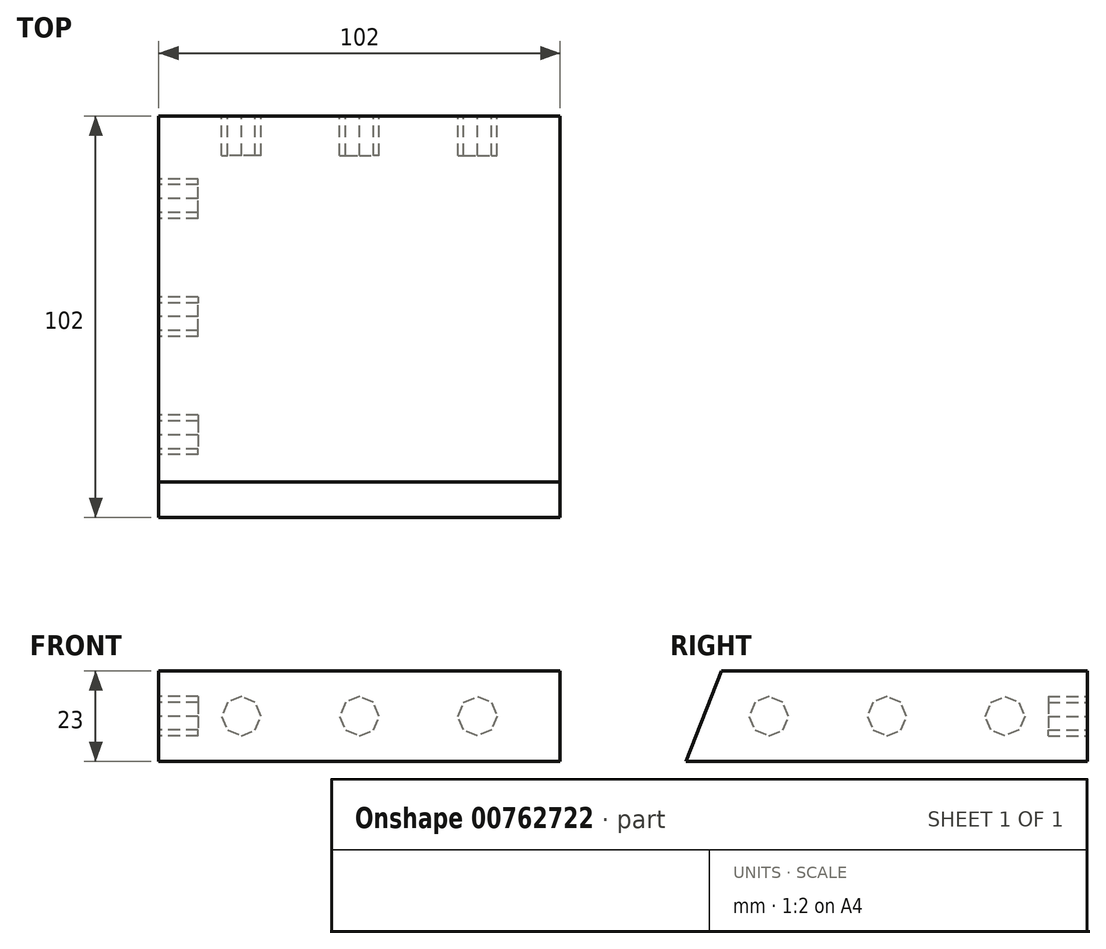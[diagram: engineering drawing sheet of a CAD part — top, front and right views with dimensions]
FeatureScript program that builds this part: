
annotation { "Feature Type Name" : "Feature", "Feature Type Description" : "" }
export const myFeature = defineFeature(function(context is Context, id is Id, definition is map)
    precondition{}
    {
        {
            var Q0;
            Q0=qCreatedBy(makeId("Right.planeOp"),FACE);
            var sketch = newSketch(context, id + "F0", { "sketchPlane" : qUnion([Q0])});
            skLineSegment(sketch, "E0.bottom", {"start": v(51, -11.5) * mm, "end": v(-51, -11.5) * mm});
            skLineSegment(sketch, "E0.top", {"start": v(51, 11.5) * mm, "end": v(-42, 11.5) * mm});
            skLineSegment(sketch, "E0.left", {"start": v(51, -11.5) * mm, "end": v(51, 11.5) * mm});
            skPoint(sketch, "E0.middle", {"position": v(0, 0) * mm});
            skLineSegment(sketch, "E1", {"start": v(-42, 11.5) * mm, "end": v(-51, -11.5) * mm});
            skPoint(sketch, "E0.right.end.orphan", {"position": v(-51, 11.5) * mm});
            skSolve(sketch);
        }
        {
            var Q0;
            Q0 = qSketchRegion(id + "F0", true);
            extrude(context, id + "F1", {"entities" : qUnion([Q0]), "endBound" : BoundingType.SYMMETRIC, "depth" : 102 * mm, "offsetDistance" : 25 * mm});
        }
        {
            var Q0;
            Q0=makeQuery(id+"F1.opExtrude","SWEPT_FACE",FACE,{"disambiguationData":[OSD([sQuery(id+"F0.wireOp",EDGE,"E0.left")])]});
            var sketch = newSketch(context, id + "F2", { "sketchPlane" : qUnion([Q0])});
            skCircle(sketch, "E2.cCircle", {"center": v(0, 0) * mm, "radius": 5 * mm, "construction": true});
            skLineSegment(sketch, "E2.0", {"start": v(0, -5) * mm, "end": v(-3.54, -3.54) * mm});
            skLineSegment(sketch, "E2.1", {"start": v(-3.54, -3.54) * mm, "end": v(-5, 0) * mm});
            skLineSegment(sketch, "E2.2", {"start": v(-5, 0) * mm, "end": v(-3.54, 3.54) * mm});
            skLineSegment(sketch, "E2.3", {"start": v(-3.54, 3.54) * mm, "end": v(0, 5) * mm});
            skLineSegment(sketch, "E2.4", {"start": v(0, 5) * mm, "end": v(3.54, 3.54) * mm});
            skLineSegment(sketch, "E2.5", {"start": v(3.54, 3.54) * mm, "end": v(5, 0) * mm});
            skLineSegment(sketch, "E2.6", {"start": v(5, 0) * mm, "end": v(3.54, -3.54) * mm});
            skLineSegment(sketch, "E2.7", {"start": v(3.54, -3.54) * mm, "end": v(0, -5) * mm});
            skLineSegment(sketch, "E3.1.0.0", {"start": v(30, 5) * mm, "end": v(33.54, 3.54) * mm});
            skLineSegment(sketch, "E3.1.0.1", {"start": v(33.54, 3.54) * mm, "end": v(35, 0) * mm});
            skLineSegment(sketch, "E3.1.0.2", {"start": v(35, 0) * mm, "end": v(33.54, -3.54) * mm});
            skLineSegment(sketch, "E3.1.0.3", {"start": v(33.54, -3.54) * mm, "end": v(30, -5) * mm});
            skLineSegment(sketch, "E3.1.0.4", {"start": v(30, -5) * mm, "end": v(26.46, -3.54) * mm});
            skLineSegment(sketch, "E3.1.0.5", {"start": v(26.46, -3.54) * mm, "end": v(25, 0) * mm});
            skLineSegment(sketch, "E3.1.0.6", {"start": v(25, 0) * mm, "end": v(26.46, 3.54) * mm});
            skLineSegment(sketch, "E3.1.0.7", {"start": v(26.46, 3.54) * mm, "end": v(30, 5) * mm});
            skLineSegment(sketch, "E3.direction1", {"start": v(0, 5) * mm, "end": v(30, 5) * mm, "construction": true});
            skLineSegment(sketch, "E4.MirrorCS", {"start": v(-26.46, 3.54) * mm, "end": v(-30, 5) * mm});
            skLineSegment(sketch, "E5.MirrorCS", {"start": v(-25, 0) * mm, "end": v(-26.46, 3.54) * mm});
            skLineSegment(sketch, "E6.MirrorCS", {"start": v(-26.46, -3.54) * mm, "end": v(-25, 0) * mm});
            skLineSegment(sketch, "E7.MirrorCS", {"start": v(-30, -5) * mm, "end": v(-26.46, -3.54) * mm});
            skLineSegment(sketch, "E8.MirrorCS", {"start": v(-33.54, -3.54) * mm, "end": v(-30, -5) * mm});
            skLineSegment(sketch, "E9.MirrorCS", {"start": v(-35, 0) * mm, "end": v(-33.54, -3.54) * mm});
            skLineSegment(sketch, "E10.MirrorCS", {"start": v(-33.54, 3.54) * mm, "end": v(-35, 0) * mm});
            skLineSegment(sketch, "E11.MirrorCS", {"start": v(-30, 5) * mm, "end": v(-33.54, 3.54) * mm});
            skSolve(sketch);
        }
        {
            var Q0;
            Q0 = qSketchRegion(id + "F2", true);
            extrude(context, id + "F3", {"entities" : qUnion([Q0]), "operationType" : NewBodyOperationType.REMOVE, "oppositeDirection" : true, "depth" : 10 * mm, "offsetDistance" : 25 * mm});
        }
        {
            var Q0;
            Q0=makeQuery(id+"F1.opExtrude","CAP_FACE",FACE,{"disambiguationData":[OSD([sQuery(id+"F0.wireOp",EDGE,"E0.bottom"),sQuery(id+"F0.wireOp",EDGE,"E0.left"),sQuery(id+"F0.wireOp",EDGE,"E0.top"),sQuery(id+"F0.wireOp",EDGE,"E1")])],"isStart":true});
            var sketch = newSketch(context, id + "F4", { "sketchPlane" : qUnion([Q0])});
            skCircle(sketch, "E12.cCircle", {"center": v(0, 0) * mm, "radius": 5 * mm, "construction": true});
            skLineSegment(sketch, "E12.0", {"start": v(0, -5) * mm, "end": v(-3.54, -3.54) * mm});
            skLineSegment(sketch, "E12.1", {"start": v(-3.54, -3.54) * mm, "end": v(-5, 0) * mm});
            skLineSegment(sketch, "E12.2", {"start": v(-5, 0) * mm, "end": v(-3.54, 3.54) * mm});
            skLineSegment(sketch, "E12.3", {"start": v(-3.54, 3.54) * mm, "end": v(0, 5) * mm});
            skLineSegment(sketch, "E12.4", {"start": v(0, 5) * mm, "end": v(3.54, 3.54) * mm});
            skLineSegment(sketch, "E12.5", {"start": v(3.54, 3.54) * mm, "end": v(5, 0) * mm});
            skLineSegment(sketch, "E12.6", {"start": v(5, 0) * mm, "end": v(3.54, -3.54) * mm});
            skLineSegment(sketch, "E12.7", {"start": v(3.54, -3.54) * mm, "end": v(0, -5) * mm});
            skLineSegment(sketch, "E13.1.0.0", {"start": v(30, 5) * mm, "end": v(33.54, 3.54) * mm});
            skLineSegment(sketch, "E13.1.0.1", {"start": v(26.46, 3.54) * mm, "end": v(30, 5) * mm});
            skLineSegment(sketch, "E13.1.0.2", {"start": v(25, 0) * mm, "end": v(26.46, 3.54) * mm});
            skLineSegment(sketch, "E13.1.0.3", {"start": v(26.46, -3.54) * mm, "end": v(25, 0) * mm});
            skLineSegment(sketch, "E13.1.0.4", {"start": v(30, -5) * mm, "end": v(26.46, -3.54) * mm});
            skLineSegment(sketch, "E13.1.0.5", {"start": v(33.54, -3.54) * mm, "end": v(30, -5) * mm});
            skLineSegment(sketch, "E13.1.0.6", {"start": v(35, 0) * mm, "end": v(33.54, -3.54) * mm});
            skLineSegment(sketch, "E13.1.0.7", {"start": v(33.54, 3.54) * mm, "end": v(35, 0) * mm});
            skLineSegment(sketch, "E13.direction1", {"start": v(0, 5) * mm, "end": v(30, 5) * mm, "construction": true});
            skLineSegment(sketch, "E14.MirrorCS", {"start": v(-26.46, 3.54) * mm, "end": v(-30, 5) * mm});
            skLineSegment(sketch, "E15.MirrorCS", {"start": v(-30, 5) * mm, "end": v(-33.54, 3.54) * mm});
            skLineSegment(sketch, "E16.MirrorCS", {"start": v(-33.54, 3.54) * mm, "end": v(-35, 0) * mm});
            skLineSegment(sketch, "E17.MirrorCS", {"start": v(-35, 0) * mm, "end": v(-33.54, -3.54) * mm});
            skLineSegment(sketch, "E18.MirrorCS", {"start": v(-33.54, -3.54) * mm, "end": v(-30, -5) * mm});
            skLineSegment(sketch, "E19.MirrorCS", {"start": v(-30, -5) * mm, "end": v(-26.46, -3.54) * mm});
            skLineSegment(sketch, "E20.MirrorCS", {"start": v(-26.46, -3.54) * mm, "end": v(-25, 0) * mm});
            skLineSegment(sketch, "E21.MirrorCS", {"start": v(-25, 0) * mm, "end": v(-26.46, 3.54) * mm});
            skSolve(sketch);
        }
        {
            var Q0;
            Q0 = qSketchRegion(id + "F4", true);
            extrude(context, id + "F5", {"entities" : qUnion([Q0]), "operationType" : NewBodyOperationType.REMOVE, "oppositeDirection" : true, "depth" : 10 * mm, "offsetDistance" : 25 * mm});
        }
    });
